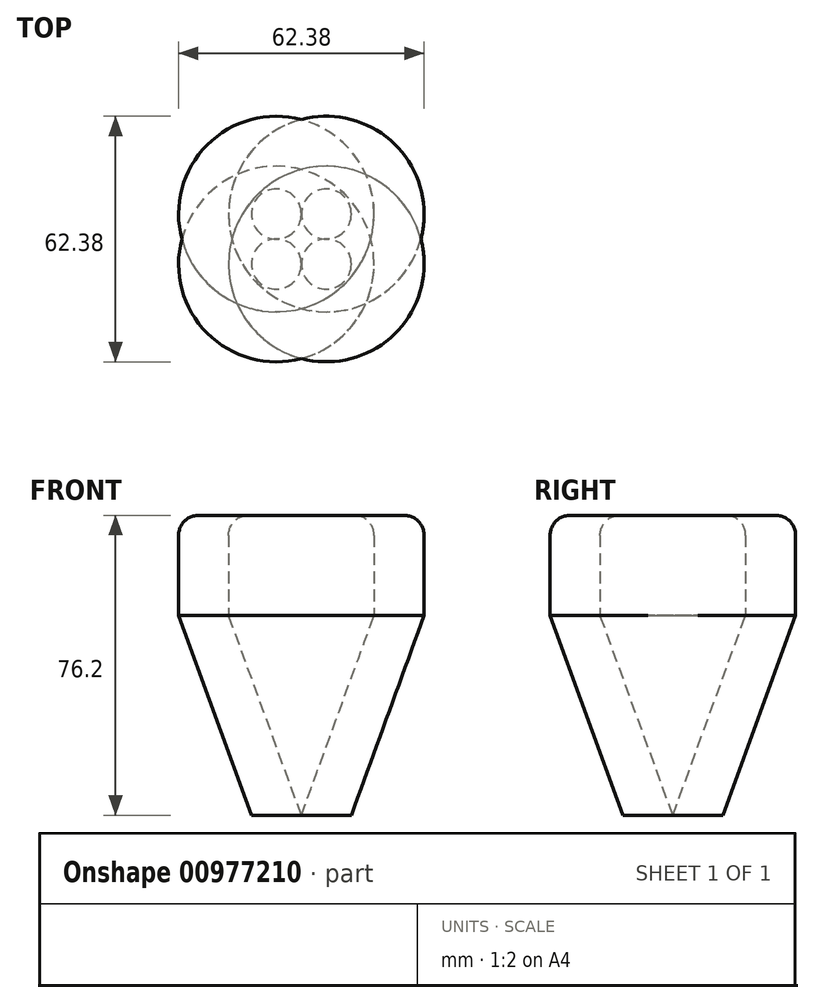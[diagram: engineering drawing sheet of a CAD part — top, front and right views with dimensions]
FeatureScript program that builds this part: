
annotation { "Feature Type Name" : "Feature", "Feature Type Description" : "" }
export const myFeature = defineFeature(function(context is Context, id is Id, definition is map)
    precondition{}
    {
        {
            var Q0;
            Q0=qCreatedBy(makeId("Top.planeOp"),FACE);
            var sketch = newSketch(context, id + "F0", { "sketchPlane" : qUnion([Q0])});
            skCircle(sketch, "E0", {"center": v(-12.7, 0) * mm, "radius": 6.35 * mm});
            skCircle(sketch, "E1", {"center": v(0, 0) * mm, "radius": 6.35 * mm});
            skCircle(sketch, "E2", {"center": v(-12.7, -12.7) * mm, "radius": 6.35 * mm});
            skCircle(sketch, "E3", {"center": v(0, -12.7) * mm, "radius": 6.35 * mm});
            skSolve(sketch);
        }
        {
            var Q0;
            {var subQ0=sQuery(id+"F0.wireOp",EDGE,"E0");var subQ1=makeQuery(id+"F0.imprint","INTERSECT",VERTEX,{"derivedFrom":[subQ0,sQuery(id+"F0.wireOp",EDGE,"E1")]});Q0=makeQuery(id+"F0.imprint","IMPRINT",FACE,{"disambiguationData":[TD([[makeQuery(id+"F0.imprint","IMPRINT",EDGE,{"disambiguationData":[TD([[subQ1,-1.0]])],"derivedFrom":subQ0}),1.0]])]});}
            var Q1;
            {var subQ0=sQuery(id+"F0.wireOp",EDGE,"E2");var subQ1=makeQuery(id+"F0.imprint","INTERSECT",VERTEX,{"derivedFrom":[sQuery(id+"F0.wireOp",EDGE,"E0"),subQ0]});Q1=makeQuery(id+"F0.imprint","IMPRINT",FACE,{"disambiguationData":[TD([[makeQuery(id+"F0.imprint","IMPRINT",EDGE,{"disambiguationData":[TD([[subQ1,1.0]])],"derivedFrom":subQ0}),1.0]])]});}
            var Q2;
            {var subQ0=sQuery(id+"F0.wireOp",EDGE,"E3");var subQ1=makeQuery(id+"F0.imprint","INTERSECT",VERTEX,{"derivedFrom":[sQuery(id+"F0.wireOp",EDGE,"E1"),subQ0]});Q2=makeQuery(id+"F0.imprint","IMPRINT",FACE,{"disambiguationData":[TD([[makeQuery(id+"F0.imprint","IMPRINT",EDGE,{"disambiguationData":[TD([[subQ1,-1.0]])],"derivedFrom":subQ0}),1.0]])]});}
            var Q3;
            {var subQ0=sQuery(id+"F0.wireOp",EDGE,"E1");var subQ1=makeQuery(id+"F0.imprint","INTERSECT",VERTEX,{"derivedFrom":[sQuery(id+"F0.wireOp",EDGE,"E0"),subQ0]});Q3=makeQuery(id+"F0.imprint","IMPRINT",FACE,{"disambiguationData":[TD([[makeQuery(id+"F0.imprint","IMPRINT",EDGE,{"disambiguationData":[TD([[subQ1,-1.0]])],"derivedFrom":subQ0}),1.0]])]});}
            extrude(context, id + "F1", {"entities" : qUnion([Q0, Q1, Q2, Q3]), "depth" : 50.8 * mm, "offsetDistance" : 25.4 * mm, "hasDraft" : true, "draftAngle" : 20 * degree});
        }
        {
            var Q0;
            Q0=makeQuery(id+"F1.opExtrude","CAP_FACE",FACE,{"disambiguationData":[OSD([sQuery(id+"F0.wireOp",EDGE,"E0")])],"isStart":false});
            var Q1;
            Q1=makeQuery(id+"F1.opExtrude","CAP_FACE",FACE,{"disambiguationData":[OSD([sQuery(id+"F0.wireOp",EDGE,"E1")])],"isStart":false});
            var Q2;
            Q2=makeQuery(id+"F1.opExtrude","CAP_FACE",FACE,{"disambiguationData":[OSD([sQuery(id+"F0.wireOp",EDGE,"E3")])],"isStart":false});
            var Q3;
            Q3=makeQuery(id+"F1.opExtrude","CAP_FACE",FACE,{"disambiguationData":[OSD([sQuery(id+"F0.wireOp",EDGE,"E2")])],"isStart":false});
            extrude(context, id + "F2", {"entities" : qUnion([Q0, Q1, Q2, Q3]), "depth" : 25.4 * mm, "offsetDistance" : 25.4 * mm});
        }
        {
            var Q0;
            Q0=makeQuery(id+"F2.opExtrude","CAP_EDGE",EDGE,{"disambiguationData":[OSD([sQuery(id+"F0.wireOp",EDGE,"E0")])],"isStart":false});
            var Q1;
            Q1=makeQuery(id+"F2.opExtrude","CAP_EDGE",EDGE,{"disambiguationData":[OSD([sQuery(id+"F0.wireOp",EDGE,"E1")])],"isStart":false});
            var Q2;
            Q2=makeQuery(id+"F2.opExtrude","CAP_EDGE",EDGE,{"disambiguationData":[OSD([sQuery(id+"F0.wireOp",EDGE,"E3")])],"isStart":false});
            var Q3;
            Q3=makeQuery(id+"F2.opExtrude","CAP_EDGE",EDGE,{"disambiguationData":[OSD([sQuery(id+"F0.wireOp",EDGE,"E2")])],"isStart":false});
            fillet(context, id + "F3", {"entities" : qUnion([Q0, Q1, Q2, Q3]), "radius" : 5.08 * mm, "tangentPropagation" : true, "allowEdgeOverflow" : false});
        }
    });
